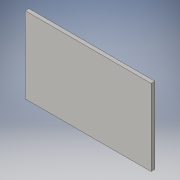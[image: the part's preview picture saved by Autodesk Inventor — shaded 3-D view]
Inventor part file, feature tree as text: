
AUTODESK INVENTOR PART (.ipt)
format: ipt  version: 2016 (Build 200138000, 138)  size: 87,040 bytes
history: native  units: in
note: dims shown in document units (in); Inventor stores cm internally (conversion verified against a paired STEP export)
features: extrude x1, sketch x1
ambient origin geometry x8: Origin, YZ Plane, XZ Plane, XY Plane, X Axis, Y Axis, Z Axis, Center Point
bodies: Solid1 (feature_tree)
feature tree (2):
  extrude  "Extrusion1"  [1 undecoded]
  sketch  "Sketch1"  dims[d3=0.0in]
note: 1 required parameter value undecoded (feature->parameter linkage not recoverable at this tier; creation-order binding heuristic only, values carry confidence <= 0.55)
